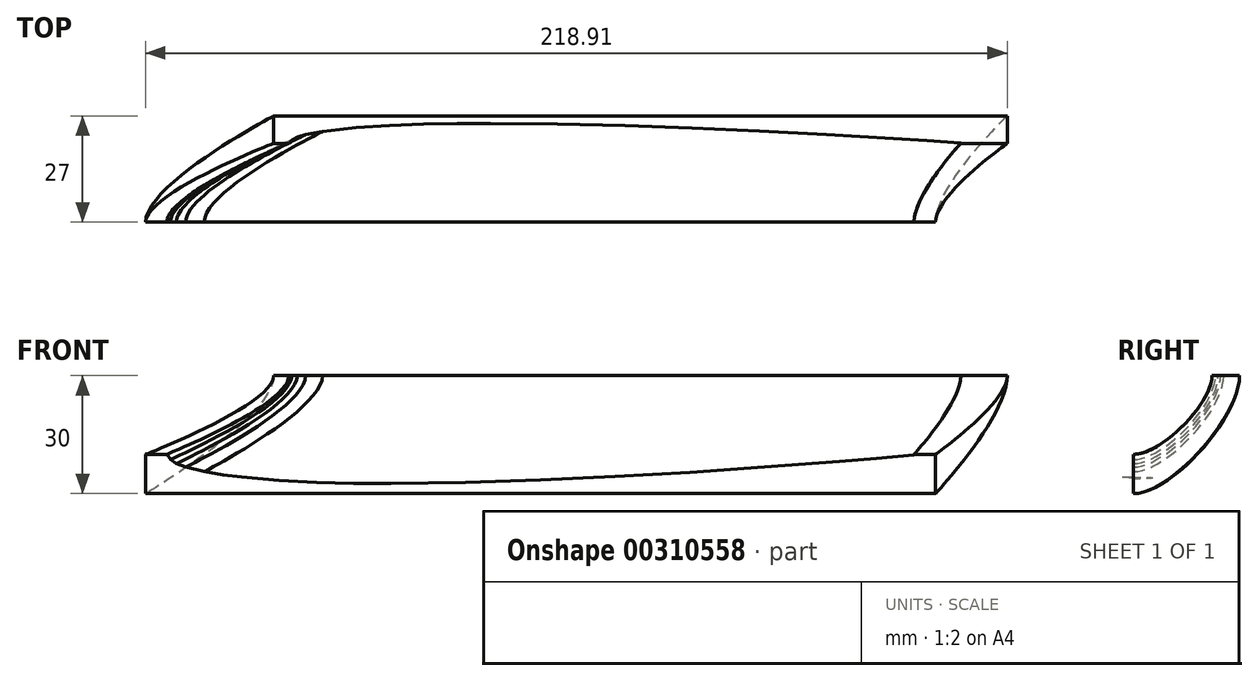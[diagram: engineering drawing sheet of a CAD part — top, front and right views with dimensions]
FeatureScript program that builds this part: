
annotation { "Feature Type Name" : "Feature", "Feature Type Description" : "" }
export const myFeature = defineFeature(function(context is Context, id is Id, definition is map)
    precondition{}
    {
        {
            var Q0;
            Q0=qCreatedBy(makeId("Top.planeOp"),FACE);
            cPlane(context, id + "F0", {"entities" : qUnion([Q0]), "cplaneType" : CPlaneType.OFFSET, "offset" : 20 * mm, "width" : 150 * mm, "height" : 150 * mm});
        }
        {
            var Q0;
            Q0=qCreatedBy(makeId("Front.planeOp"),FACE);
            var sketch = newSketch(context, id + "F1", { "sketchPlane" : qUnion([Q0])});
            skLineSegment(sketch, "E0", {"start": v(94.9, 0.16) * mm, "end": v(85.4, 1) * mm});
            skLineSegment(sketch, "E1", {"start": v(85.4, 1) * mm, "end": v(75.92, 1.8) * mm});
            skLineSegment(sketch, "E2", {"start": v(75.92, 1.8) * mm, "end": v(56.94, 3.25) * mm});
            skLineSegment(sketch, "E3", {"start": v(56.94, 3.25) * mm, "end": v(37.96, 4.54) * mm});
            skLineSegment(sketch, "E4", {"start": v(37.96, 4.54) * mm, "end": v(18.98, 5.66) * mm});
            skLineSegment(sketch, "E5", {"start": v(18.98, 5.66) * mm, "end": v(0, 6.56) * mm});
            skLineSegment(sketch, "E6", {"start": v(0, 6.56) * mm, "end": v(-18.98, 7.2) * mm});
            skLineSegment(sketch, "E7", {"start": v(-18.98, 7.2) * mm, "end": v(-37.96, 7.44) * mm});
            skLineSegment(sketch, "E8", {"start": v(-37.96, 7.44) * mm, "end": v(-47.45, 7.36) * mm});
            skLineSegment(sketch, "E9", {"start": v(-47.45, 7.36) * mm, "end": v(-56.94, 7.11) * mm});
            skLineSegment(sketch, "E10", {"start": v(-56.94, 7.11) * mm, "end": v(-66.43, 6.63) * mm});
            skLineSegment(sketch, "E11", {"start": v(-66.43, 6.63) * mm, "end": v(-75.92, 5.8) * mm});
            skLineSegment(sketch, "E12", {"start": v(-75.92, 5.8) * mm, "end": v(-80.66, 5.2) * mm});
            skLineSegment(sketch, "E13", {"start": v(-80.66, 5.2) * mm, "end": v(-85.4, 4.4) * mm});
            skLineSegment(sketch, "E14", {"start": v(-85.4, 4.4) * mm, "end": v(-90.15, 3.24) * mm});
            skLineSegment(sketch, "E15", {"start": v(-90.15, 3.24) * mm, "end": v(-92.52, 2.35) * mm});
            skLineSegment(sketch, "E16", {"start": v(-92.52, 2.35) * mm, "end": v(-94, 1.43) * mm});
            skLineSegment(sketch, "E17", {"start": v(-94, 1.43) * mm, "end": v(-94.9, 0) * mm});
            skLineSegment(sketch, "E18", {"start": v(-94.9, 0) * mm, "end": v(-94, -1.32) * mm});
            skLineSegment(sketch, "E19", {"start": v(-94, -1.32) * mm, "end": v(-92.52, -2.35) * mm});
            skLineSegment(sketch, "E20", {"start": v(-92.52, -2.35) * mm, "end": v(-90.15, -3.24) * mm});
            skLineSegment(sketch, "E21", {"start": v(-90.15, -3.24) * mm, "end": v(-85.4, -4.4) * mm});
            skLineSegment(sketch, "E22", {"start": v(-85.4, -4.4) * mm, "end": v(-80.66, -5.2) * mm});
            skLineSegment(sketch, "E23", {"start": v(-80.66, -5.2) * mm, "end": v(-75.92, -5.8) * mm});
            skLineSegment(sketch, "E24", {"start": v(-75.92, -5.8) * mm, "end": v(-66.43, -6.63) * mm});
            skLineSegment(sketch, "E25", {"start": v(-66.43, -6.63) * mm, "end": v(-56.94, -7.11) * mm});
            skLineSegment(sketch, "E26", {"start": v(-56.94, -7.11) * mm, "end": v(-47.45, -7.36) * mm});
            skLineSegment(sketch, "E27", {"start": v(-47.45, -7.36) * mm, "end": v(-37.96, -7.44) * mm});
            skLineSegment(sketch, "E28", {"start": v(-37.96, -7.44) * mm, "end": v(-18.98, -7.2) * mm});
            skLineSegment(sketch, "E29", {"start": v(-18.98, -7.2) * mm, "end": v(0, -6.56) * mm});
            skLineSegment(sketch, "E30", {"start": v(0, -6.56) * mm, "end": v(18.98, -5.66) * mm});
            skLineSegment(sketch, "E31", {"start": v(18.98, -5.66) * mm, "end": v(37.96, -4.54) * mm});
            skLineSegment(sketch, "E32", {"start": v(37.96, -4.54) * mm, "end": v(56.94, -3.25) * mm});
            skLineSegment(sketch, "E33", {"start": v(56.94, -3.25) * mm, "end": v(75.92, -1.8) * mm});
            skLineSegment(sketch, "E34", {"start": v(75.92, -1.8) * mm, "end": v(85.4, -1) * mm});
            skLineSegment(sketch, "E35", {"start": v(85.4, -1) * mm, "end": v(94.9, -0.16) * mm});
            skLineSegment(sketch, "E36", {"start": v(94.9, -0.16) * mm, "end": v(94.9, 0.16) * mm});
            skSolve(sketch);
        }
        {
            var Q0;
            Q0=qCreatedBy(id+"F0.planeOp",FACE);
            var sketch = newSketch(context, id + "F2", { "sketchPlane" : qUnion([Q0])});
            skLineSegment(sketch, "E37", {"start": v(106.78, 20.09) * mm, "end": v(98.25, 20.67) * mm});
            skLineSegment(sketch, "E38", {"start": v(98.25, 20.67) * mm, "end": v(89.72, 21.22) * mm});
            skLineSegment(sketch, "E39", {"start": v(89.72, 21.22) * mm, "end": v(72.65, 22.22) * mm});
            skLineSegment(sketch, "E40", {"start": v(72.65, 22.22) * mm, "end": v(55.58, 23.1) * mm});
            skLineSegment(sketch, "E41", {"start": v(55.58, 23.1) * mm, "end": v(38.52, 23.87) * mm});
            skLineSegment(sketch, "E42", {"start": v(38.52, 23.87) * mm, "end": v(21.45, 24.5) * mm});
            skLineSegment(sketch, "E43", {"start": v(21.45, 24.5) * mm, "end": v(4.38, 24.93) * mm});
            skLineSegment(sketch, "E44", {"start": v(4.38, 24.93) * mm, "end": v(-12.68, 25.1) * mm});
            skLineSegment(sketch, "E45", {"start": v(-12.68, 25.1) * mm, "end": v(-21.22, 25.05) * mm});
            skLineSegment(sketch, "E46", {"start": v(-21.22, 25.05) * mm, "end": v(-29.75, 24.87) * mm});
            skLineSegment(sketch, "E47", {"start": v(-29.75, 24.87) * mm, "end": v(-38.28, 24.54) * mm});
            skLineSegment(sketch, "E48", {"start": v(-38.28, 24.54) * mm, "end": v(-46.82, 23.97) * mm});
            skLineSegment(sketch, "E49", {"start": v(-46.82, 23.97) * mm, "end": v(-51.08, 23.56) * mm});
            skLineSegment(sketch, "E50", {"start": v(-51.08, 23.56) * mm, "end": v(-55.35, 23.01) * mm});
            skLineSegment(sketch, "E51", {"start": v(-55.35, 23.01) * mm, "end": v(-59.62, 22.21) * mm});
            skLineSegment(sketch, "E52", {"start": v(-59.62, 22.21) * mm, "end": v(-61.75, 21.6) * mm});
            skLineSegment(sketch, "E53", {"start": v(-61.75, 21.6) * mm, "end": v(-63.16, 20.88) * mm});
            skLineSegment(sketch, "E54", {"start": v(-63.16, 20.88) * mm, "end": v(-63.88, 19.98) * mm});
            skLineSegment(sketch, "E55", {"start": v(-63.88, 19.98) * mm, "end": v(-63.23, 19.07) * mm});
            skLineSegment(sketch, "E56", {"start": v(-63.23, 19.07) * mm, "end": v(-61.75, 18.37) * mm});
            skLineSegment(sketch, "E57", {"start": v(-61.75, 18.37) * mm, "end": v(-59.62, 17.75) * mm});
            skLineSegment(sketch, "E58", {"start": v(-59.62, 17.75) * mm, "end": v(-55.35, 16.95) * mm});
            skLineSegment(sketch, "E59", {"start": v(-55.35, 16.95) * mm, "end": v(-51.08, 16.4) * mm});
            skLineSegment(sketch, "E60", {"start": v(-51.08, 16.4) * mm, "end": v(-46.82, 15.99) * mm});
            skLineSegment(sketch, "E61", {"start": v(-46.82, 15.99) * mm, "end": v(-38.28, 15.42) * mm});
            skLineSegment(sketch, "E62", {"start": v(-38.28, 15.42) * mm, "end": v(-29.75, 15.09) * mm});
            skLineSegment(sketch, "E63", {"start": v(-29.75, 15.09) * mm, "end": v(-21.22, 14.91) * mm});
            skLineSegment(sketch, "E64", {"start": v(-21.22, 14.91) * mm, "end": v(-12.68, 14.86) * mm});
            skLineSegment(sketch, "E65", {"start": v(-12.68, 14.86) * mm, "end": v(4.38, 15.03) * mm});
            skLineSegment(sketch, "E66", {"start": v(4.38, 15.03) * mm, "end": v(21.45, 15.47) * mm});
            skLineSegment(sketch, "E67", {"start": v(21.45, 15.47) * mm, "end": v(38.52, 16.09) * mm});
            skLineSegment(sketch, "E68", {"start": v(38.52, 16.09) * mm, "end": v(55.58, 16.86) * mm});
            skLineSegment(sketch, "E69", {"start": v(55.58, 16.86) * mm, "end": v(72.65, 17.74) * mm});
            skLineSegment(sketch, "E70", {"start": v(72.65, 17.74) * mm, "end": v(89.72, 18.75) * mm});
            skLineSegment(sketch, "E71", {"start": v(89.72, 18.75) * mm, "end": v(98.25, 19.3) * mm});
            skLineSegment(sketch, "E72", {"start": v(98.25, 19.3) * mm, "end": v(106.78, 19.87) * mm});
            skLineSegment(sketch, "E73", {"start": v(106.78, 19.87) * mm, "end": v(106.78, 20.09) * mm});
            skSolve(sketch);
        }
        {
            var Q0;
            Q0=makeQuery(id+"F1.imprint","IMPRINT",FACE,{"disambiguationData":[TD([[makeQuery(id+"F1.imprint","IMPRINT",EDGE,{"derivedFrom":sQuery(id+"F1.wireOp",EDGE,"E0")}),1.0]])]});
            var Q1;
            Q1=makeQuery(id+"F2.imprint","IMPRINT",FACE,{"disambiguationData":[TD([[makeQuery(id+"F2.imprint","IMPRINT",EDGE,{"derivedFrom":sQuery(id+"F2.wireOp",EDGE,"E37")}),1.0]])]});
            loft(context, id + "F3", {"startCondition" : LoftEndDerivativeType.NORMAL_TO_PROFILE, "startMagnitude" : 1, "endCondition" : LoftEndDerivativeType.NORMAL_TO_PROFILE, "endMagnitude" : 1, "sheetProfilesArray" : [{ "sheetProfileEntities" : qUnion([Q0]) }, { "sheetProfileEntities" : qUnion([Q1]) }]});
        }
        {
            var Q0;
            Q0=qCreatedBy(makeId("Front.planeOp"),FACE);
            var sketch = newSketch(context, id + "F4", { "sketchPlane" : qUnion([Q0])});
            skLineSegment(sketch, "E74.bottom", {"start": v(-100.31, 0) * mm, "end": v(100.35, 0) * mm});
            skLineSegment(sketch, "E74.top", {"start": v(-100.31, -10) * mm, "end": v(100.35, -10) * mm});
            skLineSegment(sketch, "E74.left", {"start": v(-100.31, 0) * mm, "end": v(-100.31, -10) * mm});
            skLineSegment(sketch, "E74.right", {"start": v(100.35, 0) * mm, "end": v(100.35, -10) * mm});
            skLineSegment(sketch, "E75.top", {"start": v(-100.31, 10) * mm, "end": v(100.35, 10) * mm});
            skLineSegment(sketch, "E75.left", {"start": v(-100.31, 0) * mm, "end": v(-100.31, 10) * mm});
            skLineSegment(sketch, "E75.right", {"start": v(100.35, 0) * mm, "end": v(100.35, 10) * mm});
            skSolve(sketch);
        }
        {
            var Q0;
            Q0=qCreatedBy(id+"F0.planeOp",FACE);
            var sketch = newSketch(context, id + "F5", { "sketchPlane" : qUnion([Q0])});
            skLineSegment(sketch, "E76.bottom", {"start": v(-67.77, 20) * mm, "end": v(118.6, 20) * mm});
            skLineSegment(sketch, "E76.top", {"start": v(-67.77, 27) * mm, "end": v(118.6, 27) * mm});
            skLineSegment(sketch, "E76.left", {"start": v(-67.77, 20) * mm, "end": v(-67.77, 27) * mm});
            skLineSegment(sketch, "E76.right", {"start": v(118.6, 20) * mm, "end": v(118.6, 27) * mm});
            skLineSegment(sketch, "E77.bottom", {"start": v(-67.77, 20) * mm, "end": v(118.58, 20) * mm});
            skLineSegment(sketch, "E77.top", {"start": v(-67.77, 10) * mm, "end": v(118.58, 10) * mm});
            skLineSegment(sketch, "E77.left", {"start": v(-67.77, 20) * mm, "end": v(-67.77, 10) * mm});
            skLineSegment(sketch, "E77.right", {"start": v(118.58, 20) * mm, "end": v(118.58, 10) * mm});
            skSolve(sketch);
        }
        {
            var Q0;
            Q0=makeQuery(id+"F5.imprint","IMPRINT",FACE,{"disambiguationData":[TD([[makeQuery(id+"F5.imprint","IMPRINT",EDGE,{"derivedFrom":sQuery(id+"F5.wireOp",EDGE,"E76.bottom")}),1.0]])]});
            var Q1;
            Q1=makeQuery(id+"F4.imprint","IMPRINT",FACE,{"disambiguationData":[TD([[makeQuery(id+"F4.imprint","IMPRINT",EDGE,{"derivedFrom":sQuery(id+"F4.wireOp",EDGE,"E74.top")}),1.0]])]});
            loft(context, id + "F6", {"startCondition" : LoftEndDerivativeType.NORMAL_TO_PROFILE, "startMagnitude" : 1, "endCondition" : LoftEndDerivativeType.NORMAL_TO_PROFILE, "endMagnitude" : 1, "sheetProfilesArray" : [{ "sheetProfileEntities" : qUnion([Q0]) }, { "sheetProfileEntities" : qUnion([Q1]) }]});
        }
        {
            var Q0;
            Q0=makeQuery(id+"F3.opLoft","SWEPT_BODY",BODY,{"disambiguationData":[OSD([makeQuery(id+"F1.imprint","IMPRINT",FACE,{"disambiguationData":[TD([[makeQuery(id+"F1.imprint","IMPRINT",EDGE,{"derivedFrom":sQuery(id+"F1.wireOp",EDGE,"E0")}),1.0]])]}),makeQuery(id+"F2.imprint","IMPRINT",FACE,{"disambiguationData":[TD([[makeQuery(id+"F2.imprint","IMPRINT",EDGE,{"derivedFrom":sQuery(id+"F2.wireOp",EDGE,"E37")}),1.0]])]})])]});
            var Q1;
            Q1=makeQuery(id+"F6.opLoft","SWEPT_BODY",BODY,{"disambiguationData":[OSD([makeQuery(id+"F4.imprint","IMPRINT",FACE,{"disambiguationData":[TD([[makeQuery(id+"F4.imprint","IMPRINT",EDGE,{"derivedFrom":sQuery(id+"F4.wireOp",EDGE,"E74.top")}),1.0]])]}),makeQuery(id+"F5.imprint","IMPRINT",FACE,{"disambiguationData":[TD([[makeQuery(id+"F5.imprint","IMPRINT",EDGE,{"derivedFrom":sQuery(id+"F5.wireOp",EDGE,"E76.bottom")}),1.0]])]})])]});
            booleanBodies(context, id + "F7", {"operationType" : BooleanOperationType.SUBTRACTION, "tools" : qUnion([Q0]), "targets" : qUnion([Q1])});
        }
    });
